# Revit family: Shower-Door
name_source: partatom
category: Generic Models
units: mm (PartAtom-declared; Revit-internal decimal feet)

## family parameters
Always vertical = Yes
Can host rebar = No
Classification Number = 23.45.05.14.11.24
Cut with Voids When Loaded = No
Maintain Annotation Orientation = No
Part Type = Normal
Room Calculation Point = No
Round Connector Dimension = Use Diameter
Shared = No
Work Plane-Based = No

## types (20) — shared parameters
Assembly Code = C1010710
Construction Details = http://www.arcat.com
Default Elevation = 0' - 0"
Glass Thickness = 0' - 0 3/8"
Green Building-LEED = http://www.arcat.com
Handle Height = 0' - 1"
Handle Projection = 0' - 1 1/2"
Handle Radius = 0' - 1"
Hardware Material = ARCAT - Metal - Brass - BHMA605 - Bright Brass
Hinge Barrel Radius = 0' - 0 1/4"
Installed Weight_Lbs = 20
Keynote = 10820
Manufacturer = Generic
Manufacturer Fax = (203) 939-2444
Manufacturer Website = http://www.arcat.com
Model = Generic
Product Data = http://www.arcat.com
Product Properties = http://www.arcat.com
Shading Coefficent = 0.55
Specification = http://www.arcat.com
Swing Handle Height = 0' - 8"
Track Material = ARCAT - Metal - Steel - BHMA632 - Bright Brass
Visible Light Transmission = 30
zero-valued in all types: Expected Lifespan (Years), Maintenance Schedule (Months), Warranty Duration (Years)

## per-type parameters (varying)
| type | Corner Radius | Description | Door Length | DoorLoc | Height | SDLoad | Sliding Door | Swinging Door | Track Depth | Track Projection | Width |
| 72x96 Swinging | 0' - 2 1/4" | 72x96 Swinging Shower Door | 2' - 11 1/4" | 0' - 0 3/8" | 8' - 0" | 0 | No | Yes | 0' - 1 1/8" | 0' - 0 1/2" | 6' - 0" |
| 72x84 Swinging | 0' - 2 1/4" | 72x84 Swinging Shower Door | 2' - 11 1/4" | 0' - 0 3/8" | 7' - 0" | 0 | No | Yes | 0' - 1 1/8" | 0' - 0 1/2" | 6' - 0" |
| 72x72 Swinging | 0' - 2 1/4" | 72x72 Swinging Shower Door | 2' - 11 1/4" | 0' - 0 3/8" | 6' - 0" | 0 | No | Yes | 0' - 1 1/8" | 0' - 0 1/2" | 6' - 0" |
| 72x60 Swinging | 0' - 1 7/8" | 72x60 Swinging Shower Door | 2' - 11 1/4" | 0' - 0 3/8" | 5' - 0" | 0 | No | Yes | 0' - 1 1/8" | 0' - 0 1/2" | 6' - 0" |
| 72x54 Swinging | 0' - 1 11/16" | 72x54 Swinging Shower Door | 2' - 11 1/4" | 0' - 0 3/8" | 4' - 6" | 0 | No | Yes | 0' - 1 1/8" | 0' - 0 1/2" | 6' - 0" |
| 60x96 Swinging | 0' - 1 7/8" | 60x96 Swinging Shower Door | 2' - 5 1/4" | 0' - 0 3/8" | 8' - 0" | 0 | No | Yes | 0' - 1 1/8" | 0' - 0 1/2" | 5' - 0" |
| 60x84 Swinging | 0' - 1 7/8" | 60x84 Swinging Shower Door | 2' - 5 1/4" | 0' - 0 3/8" | 7' - 0" | 0 | No | Yes | 0' - 1 1/8" | 0' - 0 1/2" | 5' - 0" |
| 60x72 Swinging | 0' - 1 7/8" | 60x72 Swinging Shower Door | 2' - 5 1/4" | 0' - 0 3/8" | 6' - 0" | 0 | No | Yes | 0' - 1 1/8" | 0' - 0 1/2" | 5' - 0" |
| 60x60 Swinging | 0' - 1 7/8" | 60x60 Swinging Shower Door | 2' - 5 1/4" | 0' - 0 3/8" | 5' - 0" | 0 | No | Yes | 0' - 1 1/8" | 0' - 0 1/2" | 5' - 0" |
| 60x54 Swinging | 0' - 1 11/16" | 60x54 Swinging Shower Door | 2' - 5 1/4" | 0' - 0 3/8" | 4' - 6" | 0 | No | Yes | 0' - 1 1/8" | 0' - 0 1/2" | 5' - 0" |
| 72x96 Sliding | 0' - 2 1/4" | 72x96 Sliding Shower Door | 3' - 1 1/2" | 0' - 0 3/16" | 8' - 0" | 1 | Yes | No | 0' - 1 1/2" | 0' - 1 1/8" | 6' - 0" |
| 72x84 Sliding | 0' - 2 1/4" | 72x84 Sliding Shower Door | 3' - 1 1/2" | 0' - 0 3/16" | 7' - 0" | 1 | Yes | No | 0' - 1 1/2" | 0' - 1 1/8" | 6' - 0" |
| 72x72 Sliding | 0' - 2 1/4" | 72x72 Sliding Shower Door | 3' - 1 1/2" | 0' - 0 3/16" | 6' - 0" | 1 | Yes | No | 0' - 1 1/2" | 0' - 1 1/8" | 6' - 0" |
| 72x60 Sliding | 0' - 1 7/8" | 72x60 Sliding Shower Door | 3' - 1 1/2" | 0' - 0 3/16" | 5' - 0" | 1 | Yes | No | 0' - 1 1/2" | 0' - 1 1/8" | 6' - 0" |
| 72x54 Sliding | 0' - 1 11/16" | 72x54 Sliding Shower Door | 3' - 1 1/2" | 0' - 0 3/16" | 4' - 6" | 1 | Yes | No | 0' - 1 1/2" | 0' - 1 1/8" | 6' - 0" |
| 60x96 Sliding | 0' - 1 7/8" | 60x96 Sliding Shower Door | 2' - 7 1/2" | 0' - 0 3/16" | 8' - 0" | 1 | Yes | No | 0' - 1 1/2" | 0' - 1 1/8" | 5' - 0" |
| 60x84 Sliding | 0' - 1 7/8" | 60x84 Sliding Shower Door | 2' - 7 1/2" | 0' - 0 3/16" | 7' - 0" | 1 | Yes | No | 0' - 1 1/2" | 0' - 1 1/8" | 5' - 0" |
| 60x72 Sliding | 0' - 1 7/8" | 60x72 Sliding Shower Door | 2' - 7 1/2" | 0' - 0 3/16" | 6' - 0" | 1 | Yes | No | 0' - 1 1/2" | 0' - 1 1/8" | 5' - 0" |
| 60x60 Sliding | 0' - 1 7/8" | 60x60 Sliding Shower Door | 2' - 7 1/2" | 0' - 0 3/16" | 5' - 0" | 1 | Yes | No | 0' - 1 1/2" | 0' - 1 1/8" | 5' - 0" |
| 60x54 Sliding | 0' - 1 11/16" | 60x54 Sliding Shower Door | 2' - 7 1/2" | 0' - 0 3/16" | 4' - 6" | 1 | Yes | No | 0' - 1 1/2" | 0' - 1 1/8" | 5' - 0" |

## geometry (parser evidence)
native form markers: Sweep x4
no freeform markers — native parametric forms only
